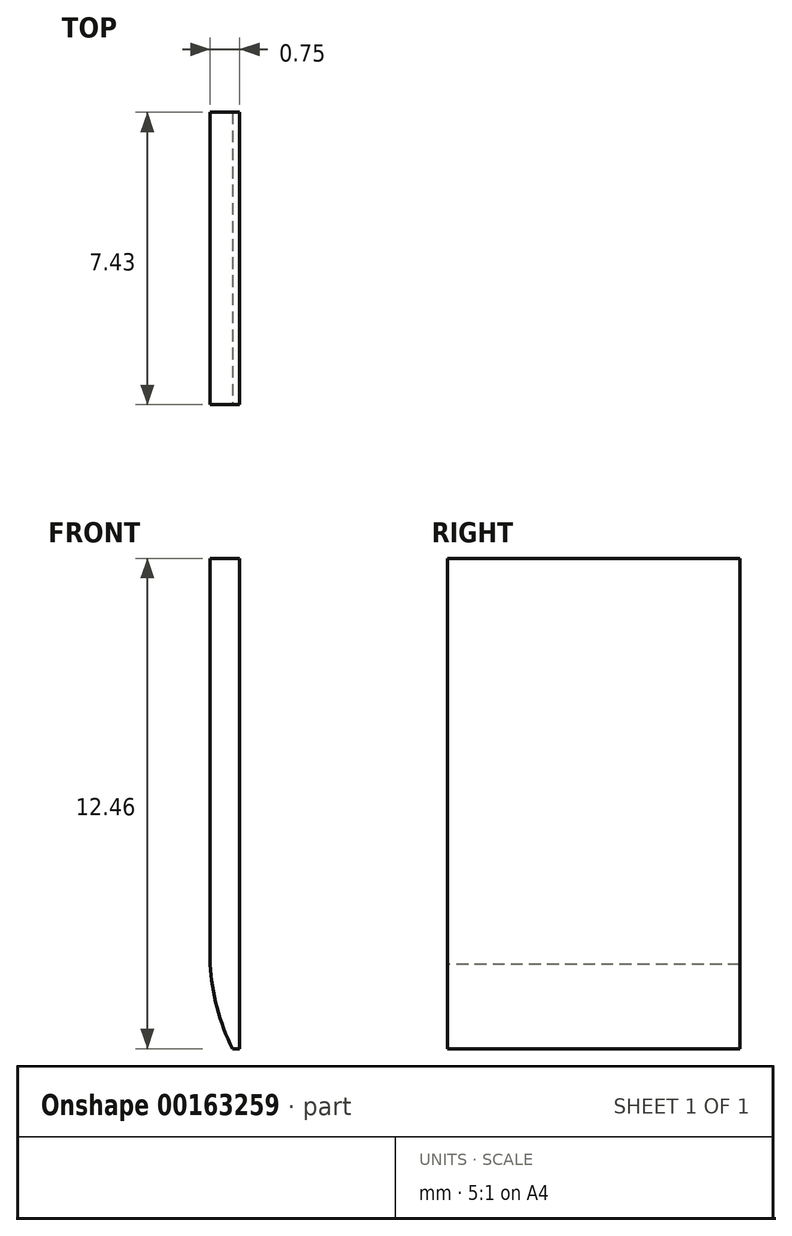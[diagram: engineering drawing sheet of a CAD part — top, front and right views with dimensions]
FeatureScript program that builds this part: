
annotation { "Feature Type Name" : "Feature", "Feature Type Description" : "" }
export const myFeature = defineFeature(function(context is Context, id is Id, definition is map)
    precondition{}
    {
        {
            var Q0;
            Q0=qCreatedBy(makeId("Right.planeOp"),FACE);
            var sketch = newSketch(context, id + "F0", { "sketchPlane" : qUnion([Q0])});
            skLineSegment(sketch, "E0.bottom", {"start": v(0.41, 0) * mm, "end": v(7.84, 0) * mm});
            skLineSegment(sketch, "E0.top", {"start": v(0.41, 12.46) * mm, "end": v(7.84, 12.46) * mm});
            skLineSegment(sketch, "E0.left", {"start": v(0.41, 0) * mm, "end": v(0.41, 12.46) * mm});
            skLineSegment(sketch, "E0.right", {"start": v(7.84, 0) * mm, "end": v(7.84, 12.46) * mm});
            skSolve(sketch);
        }
        {
            var Q0;
            Q0 = qSketchRegion(id + "F0", true);
            extrude(context, id + "F1", {"entities" : qUnion([Q0]), "depth" : .75 * mm});
        }
        {
            var Q0;
            Q0=makeQuery(id+"F1.opExtrude","SWEPT_FACE",FACE,{"disambiguationData":[OSD([sQuery(id+"F0.wireOp",EDGE,"E0.left")])]});
            var sketch = newSketch(context, id + "F2", { "sketchPlane" : qUnion([Q0])});
            skArc(sketch, "E1", {"start": v(0, 2.15) * mm, "mid": v(0.17, 1.04) * mm, "end": v(0.57, 0) * mm});
            skLineSegment(sketch, "E2", {"start": v(0, 2.15) * mm, "end": v(0, 0) * mm});
            skLineSegment(sketch, "E3", {"start": v(0, 0) * mm, "end": v(0.57, 0) * mm});
            skSolve(sketch);
        }
        {
            var Q0;
            Q0 = qSketchRegion(id + "F2", true);
            extrude(context, id + "F3", {"entities" : qUnion([Q0]), "operationType" : NewBodyOperationType.REMOVE, "endBound" : BoundingType.THROUGH_ALL, "oppositeDirection" : true, "depth" : 25 * mm});
        }
    });
